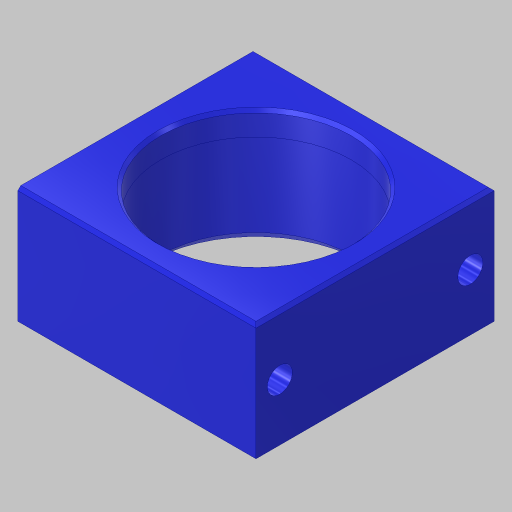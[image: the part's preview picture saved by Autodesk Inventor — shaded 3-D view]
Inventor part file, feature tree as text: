
AUTODESK INVENTOR PART (.ipt)
format: ipt  version: 2023.5 (Build 275446000, 446)  size: 187,392 bytes
history: native  units: in
note: dims shown in document units (in); Inventor stores cm internally (conversion verified against a paired STEP export)
features: extrude x3, sketch x3, chamfer x2, plane x1, mirror x1
ambient origin geometry x8: Origin, YZ Plane, XZ Plane, XY Plane, X Axis, Y Axis, Z Axis, Center Point
bodies: Solid1 (feature_tree)
feature tree (10):
  extrude  "Extrusion1"  Depth=2.5in
  extrude  "Extrusion2"  Depth=1.0in
  chamfer  "Chamfer1"  Distance=1.0in
  plane  "Work Plane1"
  extrude  "Extrusion4"  Depth=2.5in
  mirror  "Mirror1"
  chamfer  "Chamfer3"  Distance=2.0in
  sketch  "Sketch1"  dims[d0=2.0in d1=2.5in]
  sketch  "Sketch2"  dims[d2=0.25in d3=0.0in d4=2.02in d5=1.0in d6=0.0in]
  sketch  "Sketch5"  dims[d21=0.125in d22=0.125in d23=45.0deg d27=2.5in d28=2.0in d29=0.2638in d30=1.0in d31=0.0in d32=0.0312in d33=0.125in d34=45.0deg]
